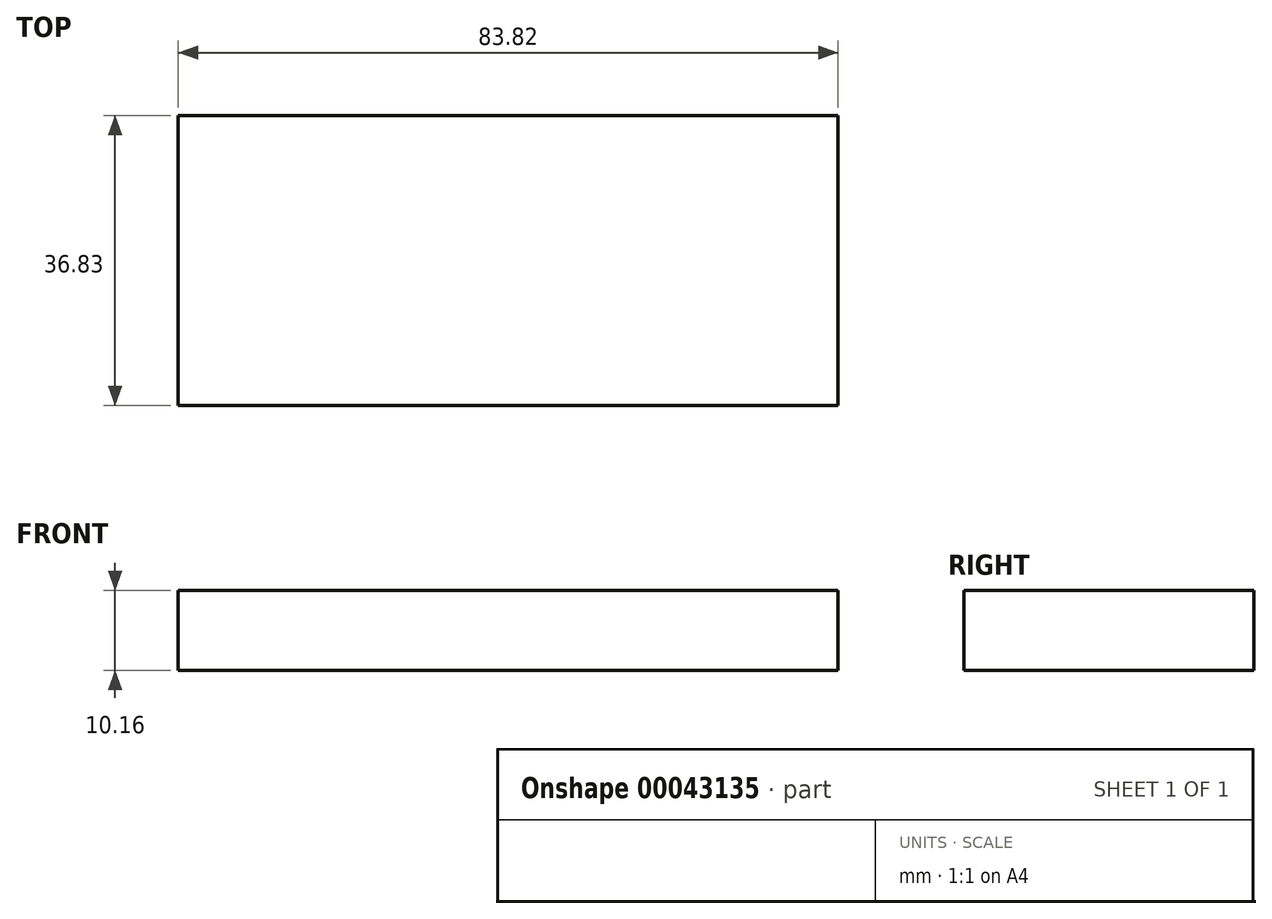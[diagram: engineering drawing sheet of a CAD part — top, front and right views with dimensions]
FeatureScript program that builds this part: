
annotation { "Feature Type Name" : "Feature", "Feature Type Description" : "" }
export const myFeature = defineFeature(function(context is Context, id is Id, definition is map)
    precondition{}
    {
        {
            var Q0;
            Q0=qCreatedBy(makeId("Top.planeOp"),FACE);
            var sketch = newSketch(context, id + "F0", { "sketchPlane" : qUnion([Q0])});
            skLineSegment(sketch, "E0.bottom", {"start": v(0, 0) * mm, "end": v(83.82, 0) * mm});
            skLineSegment(sketch, "E0.top", {"start": v(0, 36.83) * mm, "end": v(83.82, 36.83) * mm});
            skLineSegment(sketch, "E0.left", {"start": v(0, 0) * mm, "end": v(0, 36.83) * mm});
            skLineSegment(sketch, "E0.right", {"start": v(83.82, 0) * mm, "end": v(83.82, 36.83) * mm});
            skSolve(sketch);
        }
        {
            var Q0;
            Q0 = qSketchRegion(id + "F0", true);
            extrude(context, id + "F1", {"entities" : qUnion([Q0]), "depth" : 10.16 * mm});
        }
    });
